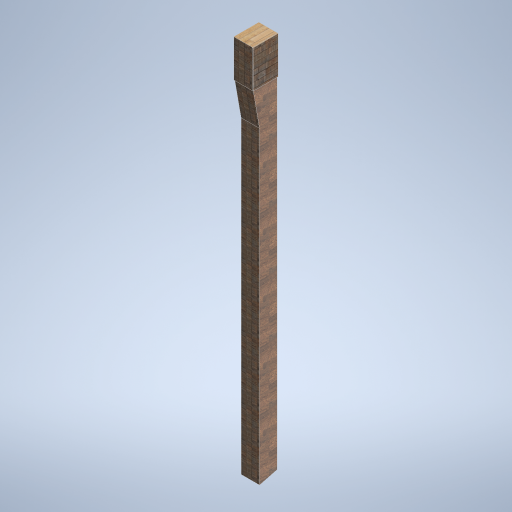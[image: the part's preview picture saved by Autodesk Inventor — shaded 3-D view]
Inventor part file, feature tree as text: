
AUTODESK INVENTOR PART (.ipt)
format: ipt  version: 2024.2 (Build 282272000, 272)  size: 321,536 bytes
history: native  units: in
note: dims shown in document units (in); Inventor stores cm internally (conversion verified against a paired STEP export)
features: other x3, sketch x1
ambient origin geometry x8: Origin, YZ Plane, XZ Plane, XY Plane, X Axis, Y Axis, Z Axis, Center Point
bodies: Solid1 (feature_tree)
feature tree (4):
  other  "side_pillar_02.ipt"
  other  "Solid1::side_pillar_02.ipt"
  other  "TaggingFeature1"
  sketch  "Sketch3"  dims[d0=0.3937in]
